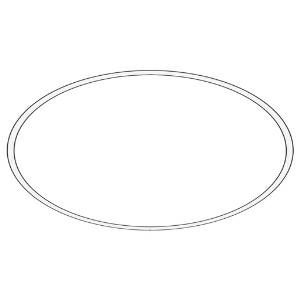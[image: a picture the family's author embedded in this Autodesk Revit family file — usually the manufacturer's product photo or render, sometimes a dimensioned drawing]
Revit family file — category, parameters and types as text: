
# Revit family: glorious_slim_210-2110
name_source: partatom
category: Leuchten
revit_build: Autodesk Revit 2016 (Build: 20190508_0715(x64)
units: mm (PartAtom-declared; Revit-internal decimal feet)

## family parameters
Basisbauteil = Fläche
Beim Laden mit Abzugskörper schneiden = Nein
Bemaßung runder Anschluss = Durchmesser verwenden
Gemeinsam genutzt = Nein
Lichtquelle = Nein
Raumberechnungspunkt = Nein
Teiletyp = Normal

## types (1)
- 210-2110-D01-H27 (4 x LED, 405.68 lm, 3.1 W, 2700K)
    Beschreibung = GLORIOUS SLIM
    CIE Flux Codes = 48 79 96 100 78
    Color Rendering = 1A/90…99
    Color Temperature = 2700K
    Height = 0 mm  [stored 0 ft]
    Hersteller = Prolicht
    Lamp Light Flux = 405.68 lm
    Lamp Power = 3.1 W
    Lamp count = 4
    Lampe = 4 x LED
    Length = 576 mm
    Luminous efficacy = 103 lm/W
    ModVariant = Nein
    Modell = 210-2110
    Mounting Place = Ceiling
    Mounting Type = Recessed
    Number of Poles = 1
    OnlyDefault = Ja
    Power Factor = 1
    Product Name = GLORIOUS SLIM
    Product group = Recessed lights
    ProductGroupID = 421
    Protection Class = Protection class
    Protection Degree = Degree of protection
    RLX_Detail_Level = 1
    RlxData = <blob elided: 68197 chars, md5=33e3107b>
    Scheinlast = 198 VA
    Socket = socket
    Standby Power = 0 W
    System Light Flux = 20355 lm
    System Power = 198 W
    Typenbild = 210-2110.jpg
    Typenkommentare = DIFFUSER Opal (01),LED COLOUR DIR 2700 K (27)
    URL = http://relux.com
    VarID = 210-2110-d01-h27
    Voltage = 0 V
    Vorgabe-Ansicht = 1800 mm
    Weight = 0.00 kg
    Width = 61 mm

note: [stored X ft] marks values corroborated as IEEE doubles in the binary element streams (Revit-internal decimal feet)

## geometry (parser evidence)
native form markers: Sweep x45
no freeform markers — native parametric forms only
